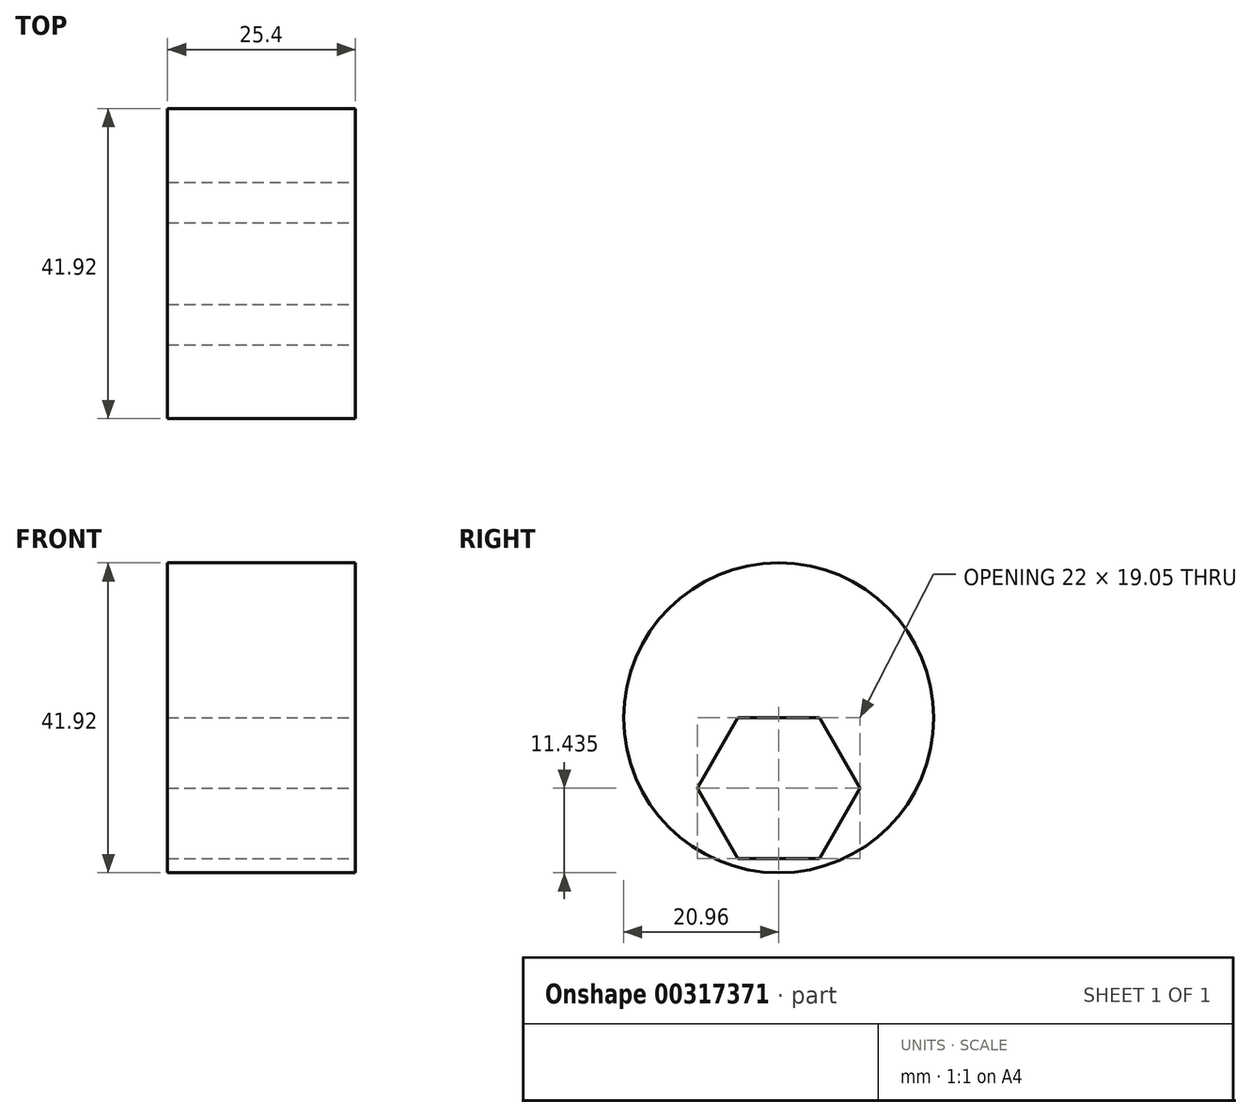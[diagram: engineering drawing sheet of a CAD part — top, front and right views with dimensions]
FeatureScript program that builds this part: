
annotation { "Feature Type Name" : "Feature", "Feature Type Description" : "" }
export const myFeature = defineFeature(function(context is Context, id is Id, definition is map)
    precondition{}
    {
        {
            var Q0;
            Q0=qCreatedBy(makeId("Right.planeOp"),FACE);
            var sketch = newSketch(context, id + "F0", { "sketchPlane" : qUnion([Q0])});
            skCircle(sketch, "E0", {"center": v(0, 0) * mm, "radius": 20.96 * mm});
            skSolve(sketch);
        }
        {
            var Q0;
            Q0=makeQuery(id+"F0.imprint","IMPRINT",FACE,{"disambiguationData":[TD([[makeQuery(id+"F0.imprint","IMPRINT",EDGE,{"derivedFrom":sQuery(id+"F0.wireOp",EDGE,"E0")}),1.0]])]});
            extrude(context, id + "F1", {"entities" : qUnion([Q0]), "depth" : 25.4 * mm});
        }
        {
            var Q0;
            Q0=makeQuery(id+"F1.opExtrude","CAP_FACE",FACE,{"disambiguationData":[OSD([sQuery(id+"F0.wireOp",EDGE,"E0")])],"isStart":false});
            var sketch = newSketch(context, id + "F2", { "sketchPlane" : qUnion([Q0])});
            skLineSegment(sketch, "E1", {"start": v(0, 0) * mm, "end": v(0, -19.05) * mm});
            skLineSegment(sketch, "E2", {"start": v(0, -19.05) * mm, "end": v(0, -9.53) * mm});
            skCircle(sketch, "E3.cCircle", {"center": v(0, -9.53) * mm, "radius": 9.53 * mm, "construction": true});
            skLineSegment(sketch, "E3.0", {"start": v(-5.5, 0) * mm, "end": v(5.5, 0) * mm});
            skLineSegment(sketch, "E3.1", {"start": v(5.5, 0) * mm, "end": v(11, -9.52) * mm});
            skLineSegment(sketch, "E3.2", {"start": v(11, -9.53) * mm, "end": v(5.5, -19.05) * mm});
            skLineSegment(sketch, "E3.3", {"start": v(5.5, -19.05) * mm, "end": v(-5.5, -19.05) * mm});
            skLineSegment(sketch, "E3.4", {"start": v(-5.5, -19.05) * mm, "end": v(-11, -9.53) * mm});
            skLineSegment(sketch, "E3.5", {"start": v(-11, -9.53) * mm, "end": v(-5.5, 0) * mm});
            skPoint(sketch, "E3.0.midPoint", {"position": v(0, 0) * mm});
            skSolve(sketch);
        }
        {
            var Q0;
            {var subQ4=sQuery(id+"F2.wireOp",EDGE,"E1");Q0=makeQuery(id+"F2.imprint","IMPRINT",FACE,{"disambiguationData":[TD([[makeQuery(id+"F2.imprint","IMPRINT",EDGE,{"derivedFrom":subQ4}),-1.0]])]});}
            var Q1;
            {var subQ2=sQuery(id+"F2.wireOp",EDGE,"E1");Q1=makeQuery(id+"F2.imprint","IMPRINT",FACE,{"disambiguationData":[TD([[makeQuery(id+"F2.imprint","IMPRINT",EDGE,{"derivedFrom":subQ2}),1.0]])]});}
            extrude(context, id + "F3", {"entities" : qUnion([Q0, Q1]), "operationType" : NewBodyOperationType.REMOVE, "oppositeDirection" : true, "depth" : 25.4 * mm});
        }
    });
